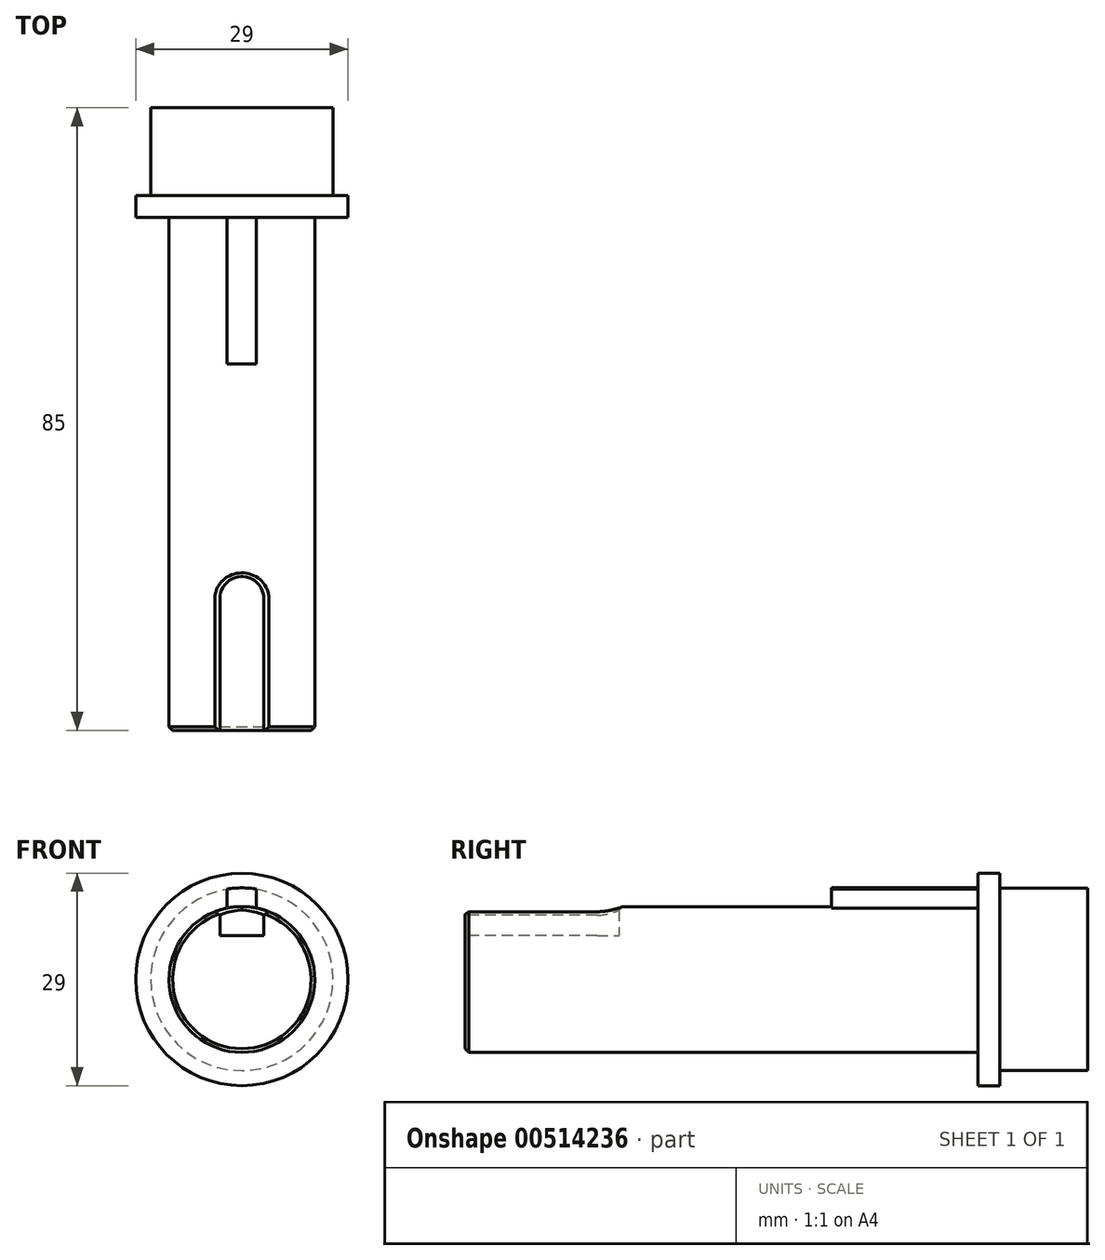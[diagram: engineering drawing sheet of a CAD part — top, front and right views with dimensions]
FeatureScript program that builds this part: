
annotation { "Feature Type Name" : "Feature", "Feature Type Description" : "" }
export const myFeature = defineFeature(function(context is Context, id is Id, definition is map)
    precondition{}
    {
        {
            var Q0;
            Q0=qCreatedBy(makeId("Front.planeOp"),FACE);
            var Q1;
            Q1=qCreatedBy(id+"FzWQQeRL8krCo04_0.planeOp",FACE);
            cPlane(context, id + "F0", {"entities" : qUnion([Q0, Q1]), "cplaneType" : CPlaneType.OFFSET, "offset" : 3 * mm, "width" : 150 * mm, "height" : 150 * mm});
        }
        {
            var Q0;
            Q0=qCreatedBy(id+"F0.planeOp",FACE);
            var sketch = newSketch(context, id + "F1", { "sketchPlane" : qUnion([Q0])});
            skCircle(sketch, "E0", {"center": v(0, 0) * mm, "radius": 14.5 * mm});
            skSolve(sketch);
        }
        {
            var Q0;
            Q0=qCreatedBy(id+"F0.planeOp",FACE);
            var sketch = newSketch(context, id + "F2", { "sketchPlane" : qUnion([Q0])});
            skCircle(sketch, "E1", {"center": v(0, 0) * mm, "radius": 9.95 * mm});
            skSolve(sketch);
        }
        {
            var Q0;
            Q0=makeQuery(id+"F1.imprint","IMPRINT",FACE,{"disambiguationData":[TD([[makeQuery(id+"F1.imprint","IMPRINT",EDGE,{"derivedFrom":sQuery(id+"F1.wireOp",EDGE,"E0")}),1.0]])]});
            extrude(context, id + "F3", {"entities" : qUnion([Q0]), "oppositeDirection" : true, "depth" : 3 * mm});
        }
        {
            var Q0;
            Q0=qCreatedBy(makeId("Front.planeOp"),FACE);
            var sketch = newSketch(context, id + "F4", { "sketchPlane" : qUnion([Q0])});
            skCircle(sketch, "E2", {"center": v(0, 0) * mm, "radius": 12.45 * mm});
            skSolve(sketch);
        }
        {
            var Q0;
            Q0 = qSketchRegion(id + "F4", true);
            extrude(context, id + "F5", {"entities" : qUnion([Q0]), "operationType" : NewBodyOperationType.ADD, "oppositeDirection" : true, "depth" : 12 * mm});
        }
        {
            var Q0;
            Q0=qCreatedBy(id+"F0.planeOp",FACE);
            var sketch = newSketch(context, id + "F6", { "sketchPlane" : qUnion([Q0])});
            skArc(sketch, "E3", {"start": v(2, 12.34) * mm, "mid": v(0, 12.5) * mm, "end": v(-2, 12.34) * mm});
            skLineSegment(sketch, "E4", {"start": v(-2, 12.34) * mm, "end": v(-2, 9.75) * mm});
            skLineSegment(sketch, "E5", {"start": v(2, 12.34) * mm, "end": v(2, 9.75) * mm});
            skArc(sketch, "E6", {"start": v(2, 9.75) * mm, "mid": v(0, 9.95) * mm, "end": v(-2, 9.75) * mm});
            skSolve(sketch);
        }
        {
            var Q0;
            Q0 = qSketchRegion(id + "F6", true);
            extrude(context, id + "F7", {"entities" : qUnion([Q0]), "operationType" : NewBodyOperationType.ADD, "depth" : 20 * mm});
        }
        {
            var Q0;
            Q0=qCreatedBy(makeId("Top.planeOp"),FACE);
            var sketch = newSketch(context, id + "F8", { "sketchPlane" : qUnion([Q0])});
            skLineSegment(sketch, "E7", {"start": v(0, 0) * mm, "end": v(0, -77.66) * mm});
            skSolve(sketch);
        }
        {
            var Q0;
            Q0=qCreatedBy(makeId("Top.planeOp"),FACE);
            cPlane(context, id + "F9", {"entities" : qUnion([Q0]), "cplaneType" : CPlaneType.OFFSET, "offset" : 6 * mm, "width" : 150 * mm, "height" : 150 * mm});
        }
        {
            var Q0;
            Q0=qCreatedBy(id+"F9.planeOp",FACE);
            var sketch = newSketch(context, id + "F10", { "sketchPlane" : qUnion([Q0])});
            skLineSegment(sketch, "E8.top", {"start": v(-3, -77) * mm, "end": v(3, -77) * mm});
            skLineSegment(sketch, "E8.left", {"start": v(-3, -55) * mm, "end": v(-3, -77) * mm});
            skLineSegment(sketch, "E8.right", {"start": v(3, -55) * mm, "end": v(3, -77) * mm});
            skArc(sketch, "E9", {"start": v(3, -55) * mm, "mid": v(0, -52) * mm, "end": v(-3, -55) * mm});
            skSolve(sketch);
        }
        {
            var Q0;
            Q0 = qSketchRegion(id + "F2", true);
            extrude(context, id + "F11", {"entities" : qUnion([Q0]), "operationType" : NewBodyOperationType.ADD, "depth" : 70 * mm});
        }
        {
            var Q0;
            Q0 = qSketchRegion(id + "F10", true);
            extrude(context, id + "F12", {"entities" : qUnion([Q0]), "operationType" : NewBodyOperationType.REMOVE, "depth" : 25 * mm});
        }
        {
            var Q0;
            Q0=makeQuery(id+"F11.opExtrude","CAP_EDGE",EDGE,{"disambiguationData":[OSD([sQuery(id+"F2.wireOp",EDGE,"E1")])],"isStart":false});
            chamfer(context, id + "F13", {"entities" : qUnion([Q0]), "width" : 0.5 * mm, "tangentPropagation" : true});
        }
        {
            var Q0;
            Q0=makeQuery(id+"F12.boolean.opBoolean","INTERSECT",EDGE,{"derivedFrom":[makeQuery(id+"F11.opExtrude","SWEPT_FACE",FACE,{"disambiguationData":[OSD([sQuery(id+"F2.wireOp",EDGE,"E1")])]}),makeQuery(id+"F12.opExtrude","SWEPT_FACE",FACE,{"disambiguationData":[OSD([sQuery(id+"F10.wireOp",EDGE,"E8.left")])]})]});
            chamfer(context, id + "F14", {"entities" : qUnion([Q0]), "width" : 0.5 * mm, "tangentPropagation" : true});
        }
    });
